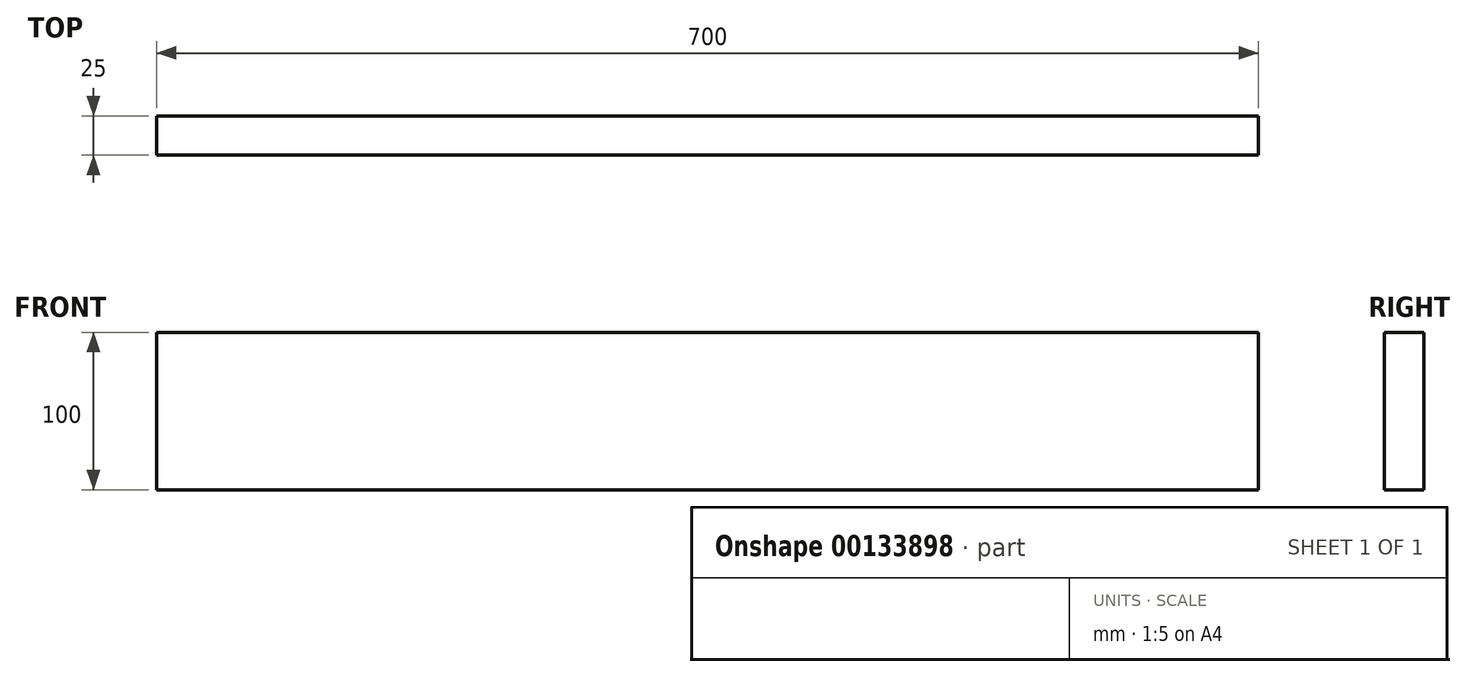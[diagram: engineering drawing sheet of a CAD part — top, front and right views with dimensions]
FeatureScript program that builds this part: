
annotation { "Feature Type Name" : "Feature", "Feature Type Description" : "" }
export const myFeature = defineFeature(function(context is Context, id is Id, definition is map)
    precondition{}
    {
        {
            var Q0;
            Q0=qCreatedBy(makeId("Front.planeOp"),FACE);
            var sketch = newSketch(context, id + "F0", { "sketchPlane" : qUnion([Q0])});
            skLineSegment(sketch, "E0.bottom", {"start": v(350, -39) * mm, "end": v(-350, -39) * mm});
            skLineSegment(sketch, "E0.top", {"start": v(350, 61) * mm, "end": v(-350, 61) * mm});
            skLineSegment(sketch, "E0.left", {"start": v(350, -39) * mm, "end": v(350, 61) * mm});
            skLineSegment(sketch, "E0.right", {"start": v(-350, -39) * mm, "end": v(-350, 61) * mm});
            skPoint(sketch, "E0.middle", {"position": v(0, 11) * mm});
            skSolve(sketch);
        }
        {
            var Q0;
            Q0=makeQuery(id+"F0.imprint","IMPRINT",FACE,{"disambiguationData":[TD([[makeQuery(id+"F0.imprint","IMPRINT",EDGE,{"derivedFrom":sQuery(id+"F0.wireOp",EDGE,"E0.bottom")}),-1.0]])]});
            extrude(context, id + "F1", {"entities" : qUnion([Q0]), "depth" : 25 * mm});
        }
    });
